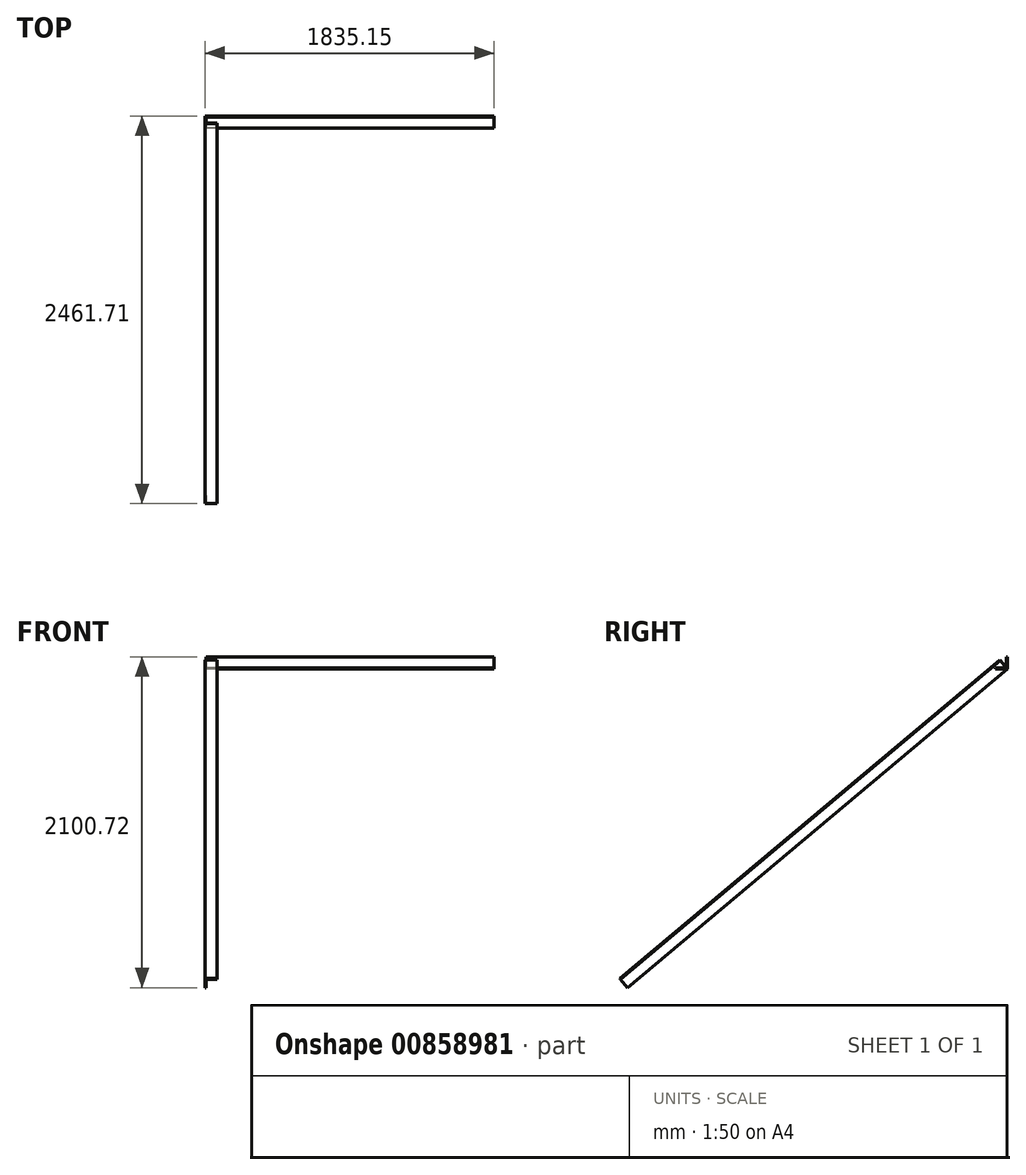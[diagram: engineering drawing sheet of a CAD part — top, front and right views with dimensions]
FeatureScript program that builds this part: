
annotation { "Feature Type Name" : "Feature", "Feature Type Description" : "" }
export const myFeature = defineFeature(function(context is Context, id is Id, definition is map)
    precondition{}
    {
        {
            var Q0;
            Q0=qCreatedBy(makeId("Right.planeOp"),FACE);
            var sketch = newSketch(context, id + "F0", { "sketchPlane" : qUnion([Q0])});
            skLineSegment(sketch, "E0", {"start": v(0, 0) * mm, "end": v(0, 76.2) * mm});
            skLineSegment(sketch, "E1", {"start": v(0, 76.2) * mm, "end": v(-6.35, 76.2) * mm});
            skLineSegment(sketch, "E2", {"start": v(-6.35, 76.2) * mm, "end": v(-6.35, 6.35) * mm});
            skLineSegment(sketch, "E3", {"start": v(-6.35, 6.35) * mm, "end": v(-76.2, 6.35) * mm});
            skLineSegment(sketch, "E4", {"start": v(-76.2, 6.35) * mm, "end": v(-76.2, 0) * mm});
            skLineSegment(sketch, "E5", {"start": v(-76.2, 0) * mm, "end": v(0, 0) * mm});
            skSolve(sketch);
        }
        {
            var Q0;
            Q0 = qSketchRegion(id + "F0", true);
            extrude(context, id + "F1", {"entities" : qUnion([Q0]), "depth" : 1828.8 * mm, "offsetDistance" : 25.4 * mm});
        }
        {
            var Q0;
            Q0=qCreatedBy(makeId("Front.planeOp"),FACE);
            var Q1;
            Q1=makeQuery(id+"F1.opExtrude","SWEPT_EDGE",EDGE,{"disambiguationData":[OSD([sQuery(id+"F0.wireOp",EDGE,"E0"),sQuery(id+"F0.wireOp",EDGE,"E5")])]});
            cPlane(context, id + "F2", {"entities" : qUnion([Q0, Q1]), "cplaneType" : CPlaneType.LINE_ANGLE, "offset" : 25.4 * mm, "angle" : 320 * degree, "width" : 152.4 * mm, "height" : 152.4 * mm});
        }
        {
            var Q0;
            Q0=qCreatedBy(id+"F2.planeOp",FACE);
            var sketch = newSketch(context, id + "F3", { "sketchPlane" : qUnion([Q0])});
            skLineSegment(sketch, "E6", {"start": v(6.35, 0) * mm, "end": v(0, 0) * mm});
            skLineSegment(sketch, "E7.MirrorCS", {"start": v(6.35, 76.2) * mm, "end": v(6.35, 0) * mm});
            skLineSegment(sketch, "E8.MirrorCS", {"start": v(0, 0) * mm, "end": v(0, 69.85) * mm});
            skLineSegment(sketch, "E9", {"start": v(6.35, 76.2) * mm, "end": v(-69.85, 76.2) * mm});
            skLineSegment(sketch, "E10", {"start": v(-69.85, 76.2) * mm, "end": v(-69.85, 69.85) * mm});
            skLineSegment(sketch, "E11", {"start": v(-69.85, 69.85) * mm, "end": v(0, 69.85) * mm});
            skSolve(sketch);
        }
        {
            var Q0;
            Q0 = qSketchRegion(id + "F3", true);
            extrude(context, id + "F4", {"entities" : qUnion([Q0]), "operationType" : NewBodyOperationType.ADD, "oppositeDirection" : true, "depth" : 3149.6 * mm, "offsetDistance" : 25.4 * mm});
        }
    });
